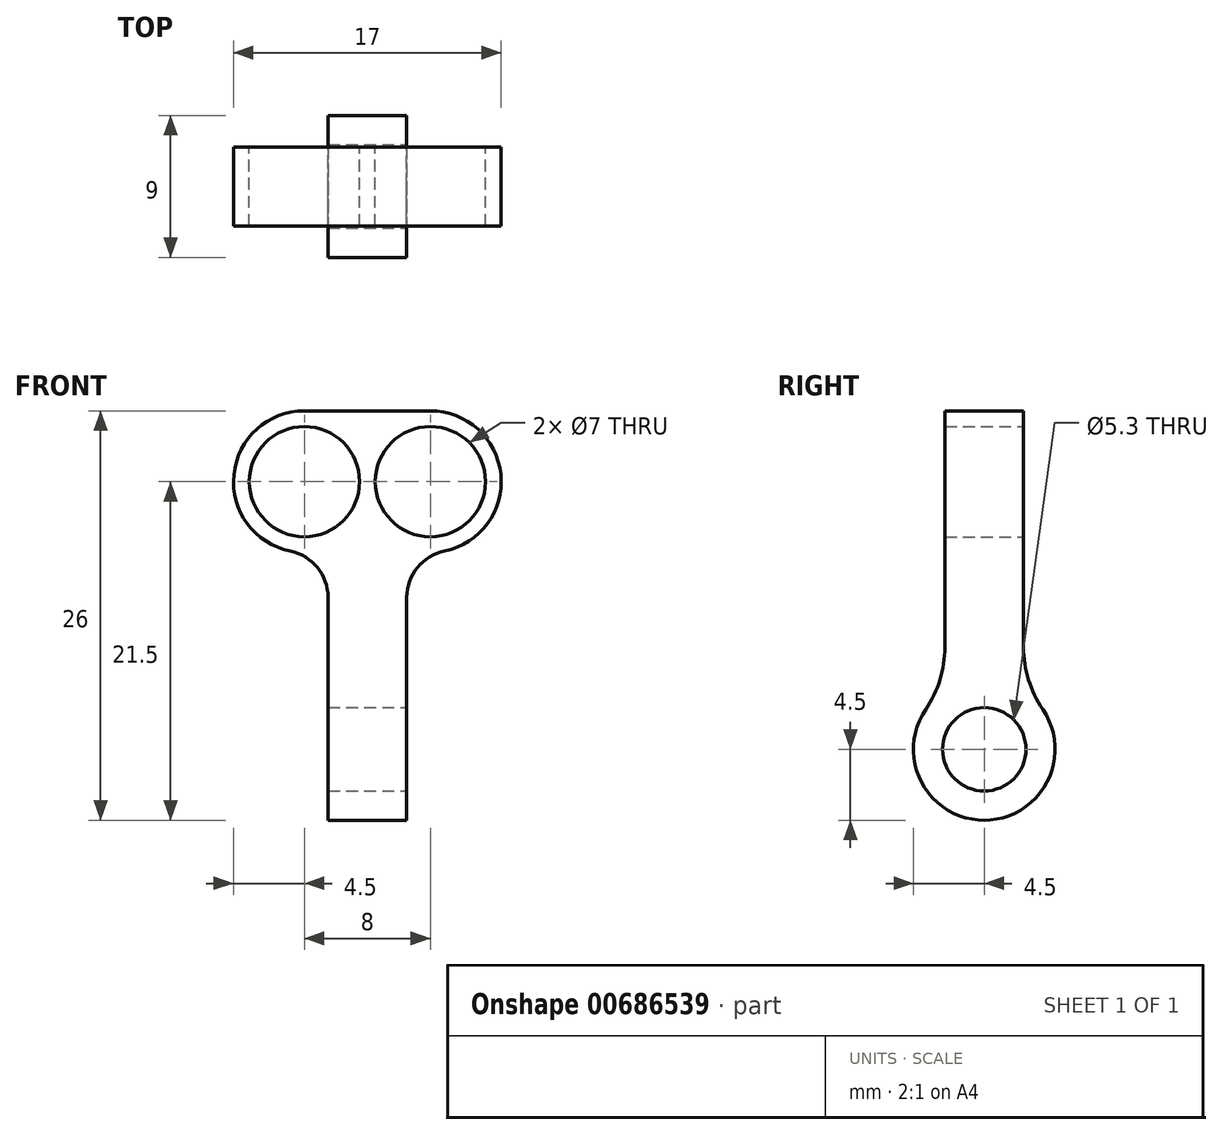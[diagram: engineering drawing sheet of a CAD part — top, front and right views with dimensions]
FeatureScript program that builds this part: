
annotation { "Feature Type Name" : "Feature", "Feature Type Description" : "" }
export const myFeature = defineFeature(function(context is Context, id is Id, definition is map)
    precondition{}
    {
        {
            var Q0;
            Q0=qCreatedBy(makeId("Front.planeOp"),FACE);
            var sketch = newSketch(context, id + "F0", { "sketchPlane" : qUnion([Q0])});
            skLineSegment(sketch, "E0.bottom", {"start": v(2.5, 12.5) * mm, "end": v(-2.5, 12.5) * mm});
            skLineSegment(sketch, "E0.top", {"start": v(2.5, -12.5) * mm, "end": v(-2.5, -12.5) * mm});
            skLineSegment(sketch, "E0.left", {"start": v(2.5, 12.5) * mm, "end": v(2.5, -12.5) * mm});
            skLineSegment(sketch, "E0.right", {"start": v(-2.5, 12.5) * mm, "end": v(-2.5, -12.5) * mm});
            skPoint(sketch, "E0.middle", {"position": v(0, 0) * mm});
            skLineSegment(sketch, "E1.bottom", {"start": v(-8.5, 12.5) * mm, "end": v(8.5, 12.5) * mm});
            skLineSegment(sketch, "E1.top", {"start": v(-8.5, 3.5) * mm, "end": v(8.5, 3.5) * mm});
            skLineSegment(sketch, "E1.left", {"start": v(-8.5, 12.5) * mm, "end": v(-8.5, 3.5) * mm});
            skLineSegment(sketch, "E1.right", {"start": v(8.5, 12.5) * mm, "end": v(8.5, 3.5) * mm});
            skCircle(sketch, "E2", {"center": v(-4, 8) * mm, "radius": 3.5 * mm});
            skCircle(sketch, "E3", {"center": v(4, 8) * mm, "radius": 3.5 * mm});
            skSolve(sketch);
        }
        {
            var Q0;
            {var subQ0=sQuery(id+"F0.wireOp",EDGE,"E1.right");Q0=makeQuery(id+"F0.imprint","IMPRINT",FACE,{"disambiguationData":[TD([[makeQuery(id+"F0.imprint","IMPRINT",EDGE,{"derivedFrom":subQ0}),-1.0]])]});}
            var Q1;
            {var subQ3=sQuery(id+"F0.wireOp",EDGE,"E1.left");Q1=makeQuery(id+"F0.imprint","IMPRINT",FACE,{"disambiguationData":[TD([[makeQuery(id+"F0.imprint","IMPRINT",EDGE,{"derivedFrom":subQ3}),1.0]])]});}
            var Q2;
            {var subQ6=sQuery(id+"F0.wireOp",EDGE,"E1.bottom");var subQ8=sQuery(id+"F0.wireOp",EDGE,"E0.left");var subQ12=makeQuery(id+"F0.imprint","INTERSECT",VERTEX,{"derivedFrom":[subQ8,subQ6]});Q2=makeQuery(id+"F0.imprint","IMPRINT",FACE,{"disambiguationData":[TD([[makeQuery(id+"F0.imprint","IMPRINT",EDGE,{"disambiguationData":[TD([[subQ12,-1.0]])],"derivedFrom":subQ8}),-1.0]])]});}
            var Q3;
            {var subQ0=sQuery(id+"F0.wireOp",EDGE,"E0.top");Q3=makeQuery(id+"F0.imprint","IMPRINT",FACE,{"disambiguationData":[TD([[makeQuery(id+"F0.imprint","IMPRINT",EDGE,{"derivedFrom":subQ0}),-1.0]])]});}
            extrude(context, id + "F1", {"entities" : qUnion([Q0, Q1, Q2, Q3]), "depth" : 5 * mm, "offsetDistance" : 25 * mm});
        }
        {
            var Q0;
            Q0=makeQuery(id+"F1.opExtrude","SWEPT_EDGE",EDGE,{"disambiguationData":[OSD([sQuery(id+"F0.wireOp",EDGE,"E1.bottom"),sQuery(id+"F0.wireOp",EDGE,"E1.right")])]});
            var Q1;
            Q1=makeQuery(id+"F1.opExtrude","SWEPT_EDGE",EDGE,{"disambiguationData":[OSD([sQuery(id+"F0.wireOp",EDGE,"E1.bottom"),sQuery(id+"F0.wireOp",EDGE,"E1.left")])]});
            var Q2;
            Q2=makeQuery(id+"F1.opExtrude","SWEPT_EDGE",EDGE,{"disambiguationData":[OSD([sQuery(id+"F0.wireOp",EDGE,"E1.top"),sQuery(id+"F0.wireOp",EDGE,"E1.right")])]});
            var Q3;
            Q3=makeQuery(id+"F1.opExtrude","SWEPT_EDGE",EDGE,{"disambiguationData":[OSD([sQuery(id+"F0.wireOp",EDGE,"E1.top"),sQuery(id+"F0.wireOp",EDGE,"E1.left")])]});
            fillet(context, id + "F2", {"entities" : qUnion([Q0, Q1, Q2, Q3]), "radius" : 4.5 * mm, "tangentPropagation" : true, "allowEdgeOverflow" : false});
        }
        {
            var Q0;
            Q0=makeQuery(id+"F1.opExtrude","CAP_EDGE",EDGE,{"disambiguationData":[OSD([sQuery(id+"F0.wireOp",EDGE,"E0.top")])],"isStart":true});
            var Q1;
            Q1=makeQuery(id+"F1.opExtrude","CAP_EDGE",EDGE,{"disambiguationData":[OSD([sQuery(id+"F0.wireOp",EDGE,"E0.top")])],"isStart":false});
            fillet(context, id + "F3", {"entities" : qUnion([Q0, Q1]), "radius" : 3.5 * mm, "tangentPropagation" : true, "allowEdgeOverflow" : false});
        }
        {
            var Q0;
            Q0=makeQuery(id+"F1.opExtrude","SWEPT_EDGE",EDGE,{"disambiguationData":[OSD([sQuery(id+"F0.wireOp",EDGE,"E0.left"),sQuery(id+"F0.wireOp",EDGE,"E1.top")])]});
            var Q1;
            Q1=makeQuery(id+"F1.opExtrude","SWEPT_EDGE",EDGE,{"disambiguationData":[OSD([sQuery(id+"F0.wireOp",EDGE,"E0.right"),sQuery(id+"F0.wireOp",EDGE,"E1.top")])]});
            fillet(context, id + "F4", {"entities" : qUnion([Q0, Q1]), "radius" : 3 * mm, "tangentPropagation" : true, "allowEdgeOverflow" : false});
        }
        {
            var Q0;
            Q0=qCreatedBy(makeId("Right.planeOp"),FACE);
            var sketch = newSketch(context, id + "F5", { "sketchPlane" : qUnion([Q0])});
            skCircle(sketch, "E4", {"center": v(-2.5, -9) * mm, "radius": 4.5 * mm});
            skSolve(sketch);
        }
        {
            var Q0;
            Q0=makeQuery(id+"F5.imprint","IMPRINT",FACE,{"disambiguationData":[TD([[makeQuery(id+"F5.imprint","IMPRINT",EDGE,{"derivedFrom":sQuery(id+"F5.wireOp",EDGE,"E4")}),1.0]])]});
            extrude(context, id + "F6", {"entities" : qUnion([Q0]), "operationType" : NewBodyOperationType.ADD, "endBound" : BoundingType.SYMMETRIC, "depth" : 5 * mm, "offsetDistance" : 25 * mm});
        }
        {
            var Q0;
            Q0=makeQuery(id+"F6.boolean.opBoolean","MERGE",FACE,{"derivedFrom":[makeQuery(id+"F1.opExtrude","SWEPT_FACE",FACE,{"disambiguationData":[OSD([sQuery(id+"F0.wireOp",EDGE,"E0.left")])]}),makeQuery(id+"F6.opExtrude","CAP_FACE",FACE,{"disambiguationData":[OSD([sQuery(id+"F5.wireOp",EDGE,"E4")])],"isStart":false})]});
            var sketch = newSketch(context, id + "F7", { "sketchPlane" : qUnion([Q0])});
            skCircle(sketch, "E5", {"center": v(-2.5, -9) * mm, "radius": 2.65 * mm});
            skSolve(sketch);
        }
        {
            var Q0;
            Q0 = qSketchRegion(id + "F7", true);
            extrude(context, id + "F8", {"entities" : qUnion([Q0]), "operationType" : NewBodyOperationType.REMOVE, "oppositeDirection" : true, "depth" : 25 * mm, "offsetDistance" : 25 * mm});
        }
        {
            var Q0;
            Q0=makeQuery(id+"F6.boolean.opBoolean","INTERSECT",EDGE,{"derivedFrom":[makeQuery(id+"F1.opExtrude","CAP_FACE",FACE,{"disambiguationData":[OSD([sQuery(id+"F0.wireOp",EDGE,"E0.top"),sQuery(id+"F0.wireOp",EDGE,"E0.left"),sQuery(id+"F0.wireOp",EDGE,"E0.right"),sQuery(id+"F0.wireOp",EDGE,"E1.bottom"),sQuery(id+"F0.wireOp",EDGE,"E1.top"),sQuery(id+"F0.wireOp",EDGE,"E1.left"),sQuery(id+"F0.wireOp",EDGE,"E1.right"),sQuery(id+"F0.wireOp",EDGE,"E2"),sQuery(id+"F0.wireOp",EDGE,"E3")])],"isStart":true}),makeQuery(id+"F6.opExtrude","SWEPT_FACE",FACE,{"disambiguationData":[OSD([sQuery(id+"F5.wireOp",EDGE,"E4")])]})]});
            var Q1;
            Q1=makeQuery(id+"F6.boolean.opBoolean","INTERSECT",EDGE,{"derivedFrom":[makeQuery(id+"F1.opExtrude","CAP_FACE",FACE,{"disambiguationData":[OSD([sQuery(id+"F0.wireOp",EDGE,"E0.top"),sQuery(id+"F0.wireOp",EDGE,"E0.left"),sQuery(id+"F0.wireOp",EDGE,"E0.right"),sQuery(id+"F0.wireOp",EDGE,"E1.bottom"),sQuery(id+"F0.wireOp",EDGE,"E1.top"),sQuery(id+"F0.wireOp",EDGE,"E1.left"),sQuery(id+"F0.wireOp",EDGE,"E1.right"),sQuery(id+"F0.wireOp",EDGE,"E2"),sQuery(id+"F0.wireOp",EDGE,"E3")])],"isStart":false}),makeQuery(id+"F6.opExtrude","SWEPT_FACE",FACE,{"disambiguationData":[OSD([sQuery(id+"F5.wireOp",EDGE,"E4")])]})]});
            fillet(context, id + "F9", {"entities" : qUnion([Q0, Q1]), "radius" : 7 * mm, "tangentPropagation" : true, "allowEdgeOverflow" : false});
        }
    });
